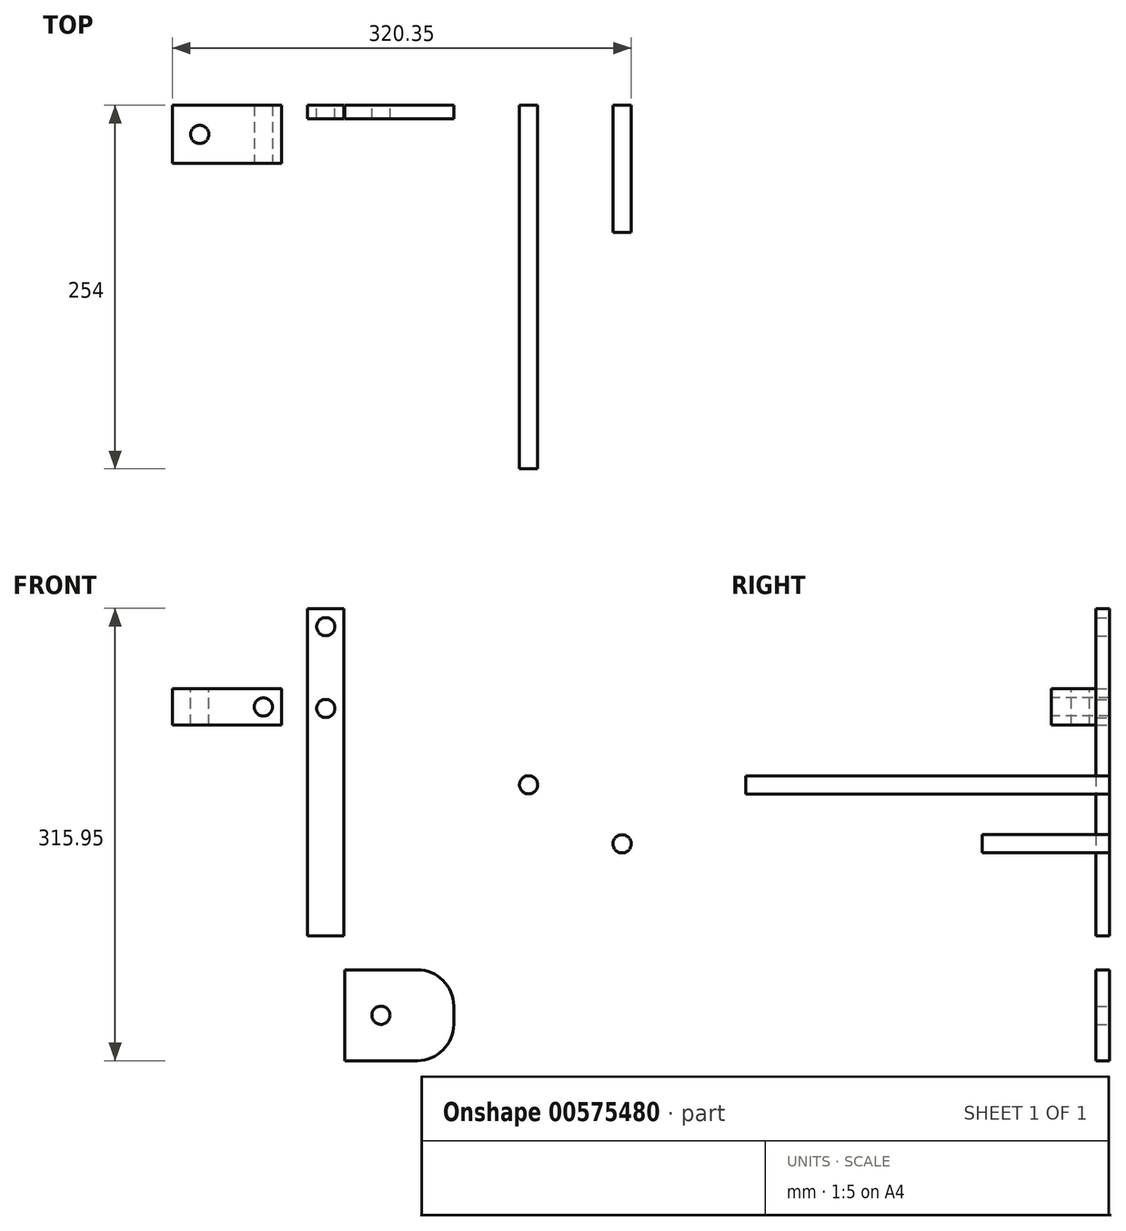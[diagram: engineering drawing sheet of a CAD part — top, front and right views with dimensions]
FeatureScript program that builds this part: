
annotation { "Feature Type Name" : "Feature", "Feature Type Description" : "" }
export const myFeature = defineFeature(function(context is Context, id is Id, definition is map)
    precondition{}
    {
        {
            var Q0;
            Q0=qCreatedBy(makeId("Front.planeOp"),FACE);
            var sketch = newSketch(context, id + "F0", { "sketchPlane" : qUnion([Q0])});
            skLineSegment(sketch, "E0.bottom", {"start": v(-201.07, 315.95) * mm, "end": v(-175.67, 315.95) * mm});
            skLineSegment(sketch, "E0.top", {"start": v(-201.07, 87.35) * mm, "end": v(-175.67, 87.35) * mm});
            skLineSegment(sketch, "E0.left", {"start": v(-201.07, 315.95) * mm, "end": v(-201.07, 87.35) * mm});
            skLineSegment(sketch, "E0.right", {"start": v(-175.67, 315.95) * mm, "end": v(-175.67, 87.35) * mm});
            skCircle(sketch, "E1", {"center": v(-188.37, 246.1) * mm, "radius": 6.35 * mm});
            skCircle(sketch, "E2", {"center": v(-188.37, 303.25) * mm, "radius": 6.35 * mm});
            skPoint(sketch, "E3", {"position": v(-188.37, 315.95) * mm});
            skSolve(sketch);
        }
        {
            var Q0;
            Q0 = qSketchRegion(id + "F0", true);
            extrude(context, id + "F1", {"entities" : qUnion([Q0]), "depth" : 9.52 * mm, "offsetDistance" : 25.4 * mm});
        }
        {
            var Q0;
            Q0=qCreatedBy(makeId("Front.planeOp"),FACE);
            var sketch = newSketch(context, id + "F2", { "sketchPlane" : qUnion([Q0])});
            skLineSegment(sketch, "E4.bottom", {"start": v(-295.41, 259.86) * mm, "end": v(-219.21, 259.86) * mm});
            skLineSegment(sketch, "E4.top", {"start": v(-295.41, 234.46) * mm, "end": v(-219.21, 234.46) * mm});
            skLineSegment(sketch, "E4.left", {"start": v(-295.41, 259.86) * mm, "end": v(-295.41, 234.46) * mm});
            skLineSegment(sketch, "E4.right", {"start": v(-219.21, 259.86) * mm, "end": v(-219.21, 234.46) * mm});
            skSolve(sketch);
        }
        {
            var Q0;
            Q0 = qSketchRegion(id + "F2", true);
            extrude(context, id + "F3", {"entities" : qUnion([Q0]), "depth" : 40.64 * mm, "offsetDistance" : 25.4 * mm});
        }
        {
            var Q0;
            Q0=makeQuery(id+"F3.opExtrude","CAP_FACE",FACE,{"disambiguationData":[OSD([sQuery(id+"F2.wireOp",EDGE,"E4.bottom"),sQuery(id+"F2.wireOp",EDGE,"E4.top"),sQuery(id+"F2.wireOp",EDGE,"E4.left"),sQuery(id+"F2.wireOp",EDGE,"E4.right")])],"isStart":false});
            var sketch = newSketch(context, id + "F4", { "sketchPlane" : qUnion([Q0])});
            skCircle(sketch, "E5", {"center": v(-231.91, 247.16) * mm, "radius": 6.35 * mm});
            skSolve(sketch);
        }
        {
            var Q0;
            Q0=makeQuery(id+"F4.imprint","IMPRINT",FACE,{"disambiguationData":[TD([[makeQuery(id+"F4.imprint","IMPRINT",EDGE,{"derivedFrom":sQuery(id+"F4.wireOp",EDGE,"E5")}),1.0]])]});
            extrude(context, id + "F5", {"entities" : qUnion([Q0]), "operationType" : NewBodyOperationType.ADD, "oppositeDirection" : true, "depth" : 57.7 * mm, "offsetDistance" : 25.4 * mm});
        }
        {
            var Q0;
            Q0=makeQuery(id+"F4.imprint","IMPRINT",FACE,{"disambiguationData":[TD([[makeQuery(id+"F4.imprint","IMPRINT",EDGE,{"derivedFrom":sQuery(id+"F4.wireOp",EDGE,"E5")}),1.0]])]});
            extrude(context, id + "F6", {"entities" : qUnion([Q0]), "operationType" : NewBodyOperationType.REMOVE, "oppositeDirection" : true, "depth" : 57.7 * mm, "offsetDistance" : 25.4 * mm});
        }
        {
            var Q0;
            Q0=makeQuery(id+"F3.opExtrude","SWEPT_FACE",FACE,{"disambiguationData":[OSD([sQuery(id+"F2.wireOp",EDGE,"E4.bottom")])]});
            var sketch = newSketch(context, id + "F7", { "sketchPlane" : qUnion([Q0])});
            skCircle(sketch, "E6", {"center": v(-276.36, -20.32) * mm, "radius": 6.35 * mm});
            skSolve(sketch);
        }
        {
            var Q0;
            Q0=makeQuery(id+"F7.imprint","IMPRINT",FACE,{"disambiguationData":[TD([[makeQuery(id+"F7.imprint","IMPRINT",EDGE,{"derivedFrom":sQuery(id+"F7.wireOp",EDGE,"E6")}),1.0]])]});
            extrude(context, id + "F8", {"entities" : qUnion([Q0]), "operationType" : NewBodyOperationType.REMOVE, "oppositeDirection" : true, "depth" : 50.8 * mm, "offsetDistance" : 25.4 * mm});
        }
        {
            var Q0;
            Q0=qCreatedBy(makeId("Front.planeOp"),FACE);
            var sketch = newSketch(context, id + "F9", { "sketchPlane" : qUnion([Q0])});
            skCircle(sketch, "E7", {"center": v(-46.7, 192.74) * mm, "radius": 6.35 * mm});
            skSolve(sketch);
        }
        {
            var Q0;
            Q0 = qSketchRegion(id + "F9", true);
            extrude(context, id + "F10", {"entities" : qUnion([Q0]), "depth" : 254 * mm, "offsetDistance" : 25.4 * mm});
        }
        {
            var Q0;
            Q0=qCreatedBy(makeId("Front.planeOp"),FACE);
            var sketch = newSketch(context, id + "F11", { "sketchPlane" : qUnion([Q0])});
            skCircle(sketch, "E8", {"center": v(18.6, 151.5) * mm, "radius": 6.35 * mm});
            skSolve(sketch);
        }
        {
            var Q0;
            Q0 = qSketchRegion(id + "F11", true);
            extrude(context, id + "F12", {"entities" : qUnion([Q0]), "depth" : 88.9 * mm, "offsetDistance" : 25.4 * mm});
        }
        {
            var Q0;
            Q0=qCreatedBy(makeId("Front.planeOp"),FACE);
            var sketch = newSketch(context, id + "F13", { "sketchPlane" : qUnion([Q0])});
            skLineSegment(sketch, "E9.bottom", {"start": v(-175.21, 63.5) * mm, "end": v(-124.41, 63.5) * mm});
            skLineSegment(sketch, "E9.top", {"start": v(-175.21, 0) * mm, "end": v(-124.41, 0) * mm});
            skLineSegment(sketch, "E9.left", {"start": v(-175.21, 63.5) * mm, "end": v(-175.21, 0) * mm});
            skLineSegment(sketch, "E9.right", {"start": v(-99.01, 38.1) * mm, "end": v(-99.01, 25.4) * mm});
            skCircle(sketch, "E10", {"center": v(-149.81, 31.75) * mm, "radius": 6.35 * mm});
            skPoint(sketch, "E11.visualSharp", {"position": v(-99.01, 63.5) * mm});
            skArc(sketch, "E11.filletArc", {"start": v(-99.01, 38.1) * mm, "mid": v(-106.45, 56.06) * mm, "end": v(-124.41, 63.5) * mm});
            skPoint(sketch, "E12.visualSharp", {"position": v(-99.01, 0) * mm});
            skArc(sketch, "E12.filletArc", {"start": v(-124.41, 0) * mm, "mid": v(-106.45, 7.44) * mm, "end": v(-99.01, 25.4) * mm});
            skSolve(sketch);
        }
        {
            var Q0;
            Q0 = qSketchRegion(id + "F13", true);
            extrude(context, id + "F14", {"entities" : qUnion([Q0]), "depth" : 9.52 * mm, "offsetDistance" : 25.4 * mm});
        }
    });
